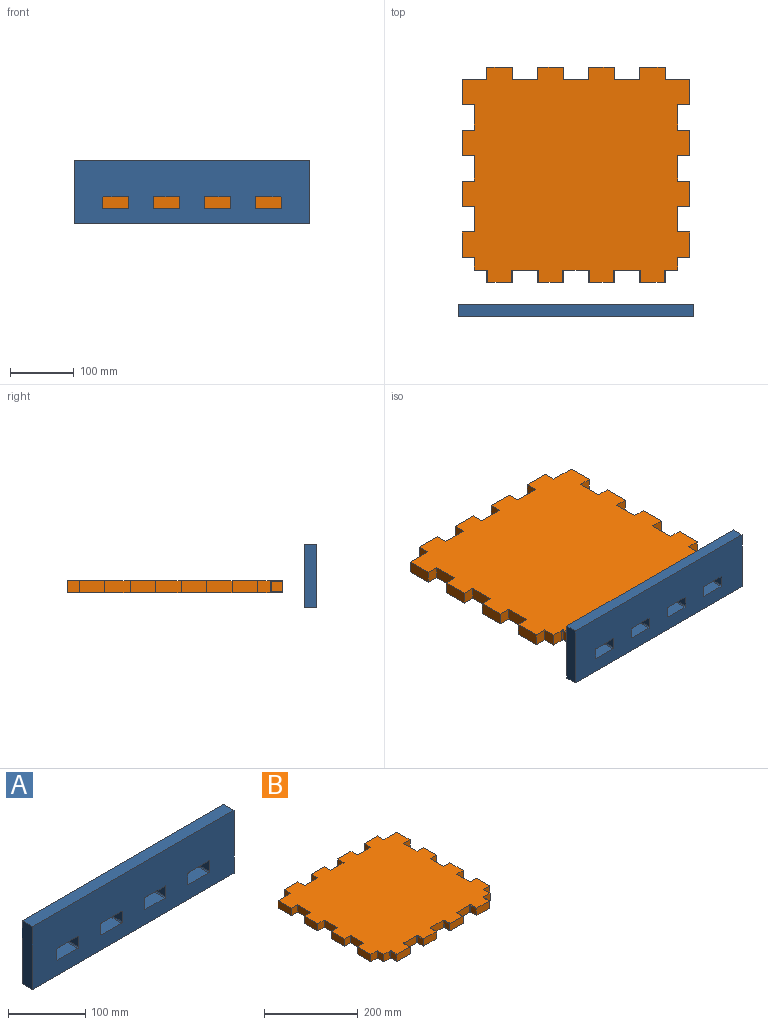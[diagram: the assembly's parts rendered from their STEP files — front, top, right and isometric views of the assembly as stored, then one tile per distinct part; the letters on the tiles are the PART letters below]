
ASSEMBLY  parts=2 mates=1
PART A: 64 faces, bbox 370x21.9x100 mm
  f0: plane 370x100mm, normal (0,-1,0), area 33967.7mm2, adj f2,f3,f4,f5,f6,f7,f8,f9
  f1: plane 370x100mm, normal (0,1,0), area 33733.9mm2, adj f2,f3,f4,f5,f6,f8,f10,f12
  f2: plane 370x19mm, normal (0,0,1), area 7030mm2, adj f0,f1,f3,f5
  f3: plane 100x19mm, normal (-1,0,0), area 1900mm2, adj f0,f1,f2,f4
  f4: plane 370x19mm, normal (0,0,-1), area 7030mm2, adj f0,f1,f3,f5
  f5: plane 100x19mm, normal (1,0,0), area 1900mm2, adj f0,f1,f2,f4
  f6: plane 37.8x19mm, normal (0,0,1), area 703.4mm2, adj f0,f1,f30,f31,f36,f37
  f7: plane 17.5x16mm, normal (-1,0,0), area 280mm2, adj f0,f28,f34,f36
  f8: plane 37.8x19mm, normal (0,0,-1), area 703.4mm2, adj f0,f1,f32,f33,f34,f35
  f9: plane 17.5x16mm, normal (1,0,0), area 280mm2, adj f0,f29,f30,f32
  f10: plane 37.8x19mm, normal (0,0,1), area 703.4mm2, adj f0,f1,f38,f39,f44,f45
  f11: plane 17.5x16mm, normal (-1,0,0), area 280mm2, adj f0,f26,f42,f44
  f12: plane 37.8x19mm, normal (0,0,-1), area 703.4mm2, adj f0,f1,f40,f41,f42,f43
  f13: plane 17.5x16mm, normal (1,0,0), area 280mm2, adj f0,f27,f38,f40
  f14: plane 37.8x19mm, normal (0,0,1), area 703.4mm2, adj f0,f1,f46,f47,f52,f53
  f15: plane 17.5x16mm, normal (-1,0,0), area 280mm2, adj f0,f24,f46,f48
  f16: plane 37.8x19mm, normal (0,0,-1), area 703.4mm2, adj f0,f1,f48,f49,f50,f51
  f17: plane 17.5x16mm, normal (1,0,0), area 280mm2, adj f0,f25,f50,f52
  f18: plane 37.8x19mm, normal (0,0,1), area 703.4mm2, adj f0,f1,f54,f55,f60,f61
  f19: plane 17.5x16mm, normal (-1,0,0), area 280mm2, adj f0,f22,f58,f60
  f20: plane 37.8x19mm, normal (0,0,-1), area 703.4mm2, adj f0,f1,f56,f57,f58,f59
  f21: plane 17.5x16mm, normal (1,0,0), area 280mm2, adj f0,f23,f54,f56
  f22: cylinder r=1.5mm len=16mm, axis (0,0,1), area 37.7mm2, adj f1,f19,f59,f61
  f23: cylinder r=1.5mm len=16mm, axis (0,0,-1), area 37.7mm2, adj f1,f21,f55,f57
  f24: cylinder r=1.5mm len=16mm, axis (0,0,1), area 37.7mm2, adj f1,f15,f47,f49
  f25: cylinder r=1.5mm len=16mm, axis (0,0,-1), area 37.7mm2, adj f1,f17,f51,f53
  f26: cylinder r=1.5mm len=16mm, axis (0,0,1), area 37.7mm2, adj f1,f11,f43,f45
  f27: cylinder r=1.5mm len=16mm, axis (0,0,-1), area 37.7mm2, adj f1,f13,f39,f41
  f28: cylinder r=1.5mm len=16mm, axis (0,0,1), area 37.7mm2, adj f1,f7,f35,f37
  f29: cylinder r=1.5mm len=16mm, axis (0,0,-1), area 37.7mm2, adj f1,f9,f31,f33
  f30: cylinder r=1.5mm len=17.5mm, axis (0,-1,0), area 41.2mm2, adj f0,f6,f9,f31
  f31: torus R=3mm, axis (0,0,1), area 4.2mm2, adj f1,f6,f29,f30
  f32: cylinder r=1.5mm len=17.5mm, axis (0,1,0), area 41.2mm2, adj f0,f8,f9,f33
  f33: torus R=3mm, axis (0,0,1), area 4.2mm2, adj f1,f8,f29,f32
  f34: cylinder r=1.5mm len=17.5mm, axis (0,-1,0), area 41.2mm2, adj f0,f7,f8,f35
  f35: torus R=3mm, axis (0,0,1), area 4.2mm2, adj f1,f8,f28,f34
  f36: cylinder r=1.5mm len=17.5mm, axis (0,1,0), area 41.2mm2, adj f0,f6,f7,f37
  f37: torus R=3mm, axis (0,0,1), area 4.2mm2, adj f1,f6,f28,f36
  f38: cylinder r=1.5mm len=17.5mm, axis (0,-1,0), area 41.2mm2, adj f0,f10,f13,f39
  f39: torus R=3mm, axis (0,0,1), area 4.2mm2, adj f1,f10,f27,f38
  f40: cylinder r=1.5mm len=17.5mm, axis (0,1,0), area 41.2mm2, adj f0,f12,f13,f41
  f41: torus R=3mm, axis (0,0,1), area 4.2mm2, adj f1,f12,f27,f40
  f42: cylinder r=1.5mm len=17.5mm, axis (0,-1,0), area 41.2mm2, adj f0,f11,f12,f43
  f43: torus R=3mm, axis (0,0,1), area 4.2mm2, adj f1,f12,f26,f42
  f44: cylinder r=1.5mm len=17.5mm, axis (0,1,0), area 41.2mm2, adj f0,f10,f11,f45
  f45: torus R=3mm, axis (0,0,1), area 4.2mm2, adj f1,f10,f26,f44
  f46: cylinder r=1.5mm len=17.5mm, axis (0,1,0), area 41.2mm2, adj f0,f14,f15,f47
  f47: torus R=3mm, axis (0,0,1), area 4.2mm2, adj f1,f14,f24,f46
  f48: cylinder r=1.5mm len=17.5mm, axis (0,-1,0), area 41.2mm2, adj f0,f15,f16,f49
  f49: torus R=3mm, axis (0,0,1), area 4.2mm2, adj f1,f16,f24,f48
  f50: cylinder r=1.5mm len=17.5mm, axis (0,1,0), area 41.2mm2, adj f0,f16,f17,f51
  f51: torus R=3mm, axis (0,0,1), area 4.2mm2, adj f1,f16,f25,f50
  f52: cylinder r=1.5mm len=17.5mm, axis (0,-1,0), area 41.2mm2, adj f0,f14,f17,f53
  f53: torus R=3mm, axis (0,0,1), area 4.2mm2, adj f1,f14,f25,f52
  f54: cylinder r=1.5mm len=17.5mm, axis (0,-1,0), area 41.2mm2, adj f0,f18,f21,f55
  f55: torus R=3mm, axis (0,0,1), area 4.2mm2, adj f1,f18,f23,f54
  f56: cylinder r=1.5mm len=17.5mm, axis (0,1,0), area 41.2mm2, adj f0,f20,f21,f57
  f57: torus R=3mm, axis (0,0,1), area 4.2mm2, adj f1,f20,f23,f56
  f58: cylinder r=1.5mm len=17.5mm, axis (0,-1,0), area 41.2mm2, adj f0,f19,f20,f59
  f59: torus R=3mm, axis (0,0,1), area 4.2mm2, adj f1,f20,f22,f58
  f60: cylinder r=1.5mm len=17.5mm, axis (0,1,0), area 41.2mm2, adj f0,f18,f19,f61
  f61: torus R=3mm, axis (0,0,1), area 4.2mm2, adj f1,f18,f22,f60
  f62: cylinder r=2.5mm len=5mm, axis (0,1,0), area 15.7mm2, adj f1,f63
  f63: plane 5x5mm, normal (0,1,0), area 19.6mm2, adj f62
PART B: 106 faces, bbox 358x338x24.8 mm
  f0: plane 19x19mm, normal (0,-1,0), area 361mm2, adj f1,f63,f64,f65
  f1: plane 20x19mm, normal (-1,0,0), area 380mm2, adj f0,f2,f64,f65
  f2: plane 19x18.9mm, normal (0,-1,0), area 351.9mm2, adj f1,f64,f65,f100,f101,f102
  f3: plane 17.5x16mm, normal (-1,0,0), area 280mm2, adj f4,f67,f75,f101
  f4: plane 40x19mm, normal (0,-1,0), area 758.1mm2, adj f3,f5,f64,f65,f66,f67,f74,f75
  f5: plane 17.5x16mm, normal (1,0,0), area 280mm2, adj f4,f66,f74,f104
  f6: plane 37.8x19mm, normal (0,-1,0), area 703.8mm2, adj f64,f65,f94,f95,f96,f103,f104,f105
  f7: plane 17.5x16mm, normal (-1,0,0), area 280mm2, adj f8,f69,f77,f95
  f8: plane 40x19mm, normal (0,-1,0), area 758.1mm2, adj f7,f9,f64,f65,f68,f69,f76,f77
  f9: plane 17.5x16mm, normal (1,0,0), area 280mm2, adj f8,f68,f76,f98
  f10: plane 37.8x19mm, normal (0,-1,0), area 703.8mm2, adj f64,f65,f88,f89,f90,f97,f98,f99
  f11: plane 17.5x16mm, normal (-1,0,0), area 280mm2, adj f12,f71,f79,f89
  f12: plane 40x19mm, normal (0,-1,0), area 758.1mm2, adj f11,f13,f64,f65,f70,f71,f78,f79
  f13: plane 17.5x16mm, normal (1,0,0), area 280mm2, adj f12,f70,f78,f92
  f14: plane 37.8x19mm, normal (0,-1,0), area 703.8mm2, adj f64,f65,f82,f83,f84,f91,f92,f93
  f15: plane 17.5x16mm, normal (-1,0,0), area 280mm2, adj f16,f73,f81,f83
  f16: plane 40x19mm, normal (0,-1,0), area 758.1mm2, adj f15,f17,f64,f65,f72,f73,f80,f81
  f17: plane 17.5x16mm, normal (1,0,0), area 280mm2, adj f16,f72,f80,f86
  f18: plane 19x18.9mm, normal (0,-1,0), area 351.9mm2, adj f19,f64,f65,f85,f86,f87
  f19: plane 20x19mm, normal (1,0,0), area 380mm2, adj f18,f20,f64,f65
  f20: plane 19x19mm, normal (0,-1,0), area 361mm2, adj f19,f21,f64,f65
  f21: plane 40x19mm, normal (1,0,0), area 760mm2, adj f20,f22,f64,f65
  f22: plane 19x19mm, normal (0,1,0), area 361mm2, adj f21,f23,f64,f65
  f23: plane 40x19mm, normal (1,0,0), area 760mm2, adj f22,f24,f64,f65
  f24: plane 19x19mm, normal (0,-1,0), area 361mm2, adj f23,f25,f64,f65
  f25: plane 40x19mm, normal (1,0,0), area 760mm2, adj f24,f26,f64,f65
  f26: plane 19x19mm, normal (0,1,0), area 361mm2, adj f25,f27,f64,f65
  f27: plane 40x19mm, normal (1,0,0), area 760mm2, adj f26,f28,f64,f65
  f28: plane 19x19mm, normal (0,-1,0), area 361mm2, adj f27,f29,f64,f65
  f29: plane 40x19mm, normal (1,0,0), area 760mm2, adj f28,f30,f64,f65
  f30: plane 19x19mm, normal (0,1,0), area 361mm2, adj f29,f31,f64,f65
  f31: plane 40x19mm, normal (1,0,0), area 760mm2, adj f30,f32,f64,f65
  f32: plane 19x19mm, normal (0,-1,0), area 361mm2, adj f31,f33,f64,f65
  f33: plane 40x19mm, normal (1,0,0), area 760mm2, adj f32,f34,f64,f65
  f34: plane 39x19mm, normal (0,1,0), area 741mm2, adj f33,f35,f64,f65
  f35: plane 19x19mm, normal (1,0,0), area 361mm2, adj f34,f36,f64,f65
  f36: plane 40x19mm, normal (0,1,0), area 760mm2, adj f35,f37,f64,f65
  f37: plane 19x19mm, normal (-1,0,0), area 361mm2, adj f36,f38,f64,f65
  f38: plane 40x19mm, normal (0,1,0), area 760mm2, adj f37,f39,f64,f65
  f39: plane 19x19mm, normal (1,0,0), area 361mm2, adj f38,f40,f64,f65
  f40: plane 40x19mm, normal (0,1,0), area 760mm2, adj f39,f41,f64,f65
  f41: plane 19x19mm, normal (-1,0,0), area 361mm2, adj f40,f42,f64,f65
  f42: plane 40x19mm, normal (0,1,0), area 760mm2, adj f41,f43,f64,f65
  f43: plane 19x19mm, normal (1,0,0), area 361mm2, adj f42,f44,f64,f65
  f44: plane 40x19mm, normal (0,1,0), area 760mm2, adj f43,f45,f64,f65
  f45: plane 19x19mm, normal (-1,0,0), area 361mm2, adj f44,f46,f64,f65
  f46: plane 40x19mm, normal (0,1,0), area 760mm2, adj f45,f47,f64,f65
  f47: plane 19x19mm, normal (1,0,0), area 361mm2, adj f46,f48,f64,f65
  f48: plane 40x19mm, normal (0,1,0), area 760mm2, adj f47,f49,f64,f65
  f49: plane 19x19mm, normal (-1,0,0), area 361mm2, adj f48,f50,f64,f65
  f50: plane 39x19mm, normal (0,1,0), area 741mm2, adj f49,f51,f64,f65
  f51: plane 40x19mm, normal (-1,0,0), area 760mm2, adj f50,f52,f64,f65
  f52: plane 19x19mm, normal (0,-1,0), area 361mm2, adj f51,f53,f64,f65
  f53: plane 40x19mm, normal (-1,0,0), area 760mm2, adj f52,f54,f64,f65
  f54: plane 19x19mm, normal (0,1,0), area 361mm2, adj f53,f55,f64,f65
  f55: plane 40x19mm, normal (-1,0,0), area 760mm2, adj f54,f56,f64,f65
  f56: plane 19x19mm, normal (0,-1,0), area 361mm2, adj f55,f57,f64,f65
  f57: plane 40x19mm, normal (-1,0,0), area 760mm2, adj f56,f58,f64,f65
  f58: plane 19x19mm, normal (0,1,0), area 361mm2, adj f57,f59,f64,f65
  f59: plane 40x19mm, normal (-1,0,0), area 760mm2, adj f58,f60,f64,f65
  f60: plane 19x19mm, normal (0,-1,0), area 361mm2, adj f59,f61,f64,f65
  f61: plane 40x19mm, normal (-1,0,0), area 760mm2, adj f60,f62,f64,f65
  f62: plane 19x19mm, normal (0,1,0), area 361mm2, adj f61,f63,f64,f65
  f63: plane 40x19mm, normal (-1,0,0), area 760mm2, adj f0,f62,f64,f65
  f64: plane 358x338mm, normal (0,0,1), area 107942.8mm2, adj f0,f1,f2,f4,f6,f8,f10,f12
  f65: plane 358x338mm, normal (0,0,-1), area 107942.8mm2, adj f0,f1,f2,f4,f6,f8,f10,f12
  f66: cylinder r=1.5mm len=17.5mm, axis (0,1,0), area 41.2mm2, adj f4,f5,f65,f103
  f67: cylinder r=1.5mm len=17.5mm, axis (0,-1,0), area 41.2mm2, adj f3,f4,f65,f100
  f68: cylinder r=1.5mm len=17.5mm, axis (0,1,0), area 41.2mm2, adj f8,f9,f65,f97
  f69: cylinder r=1.5mm len=17.5mm, axis (0,-1,0), area 41.2mm2, adj f7,f8,f65,f94
  f70: cylinder r=1.5mm len=17.5mm, axis (0,1,0), area 41.2mm2, adj f12,f13,f65,f91
  f71: cylinder r=1.5mm len=17.5mm, axis (0,-1,0), area 41.2mm2, adj f11,f12,f65,f88
  f72: cylinder r=1.5mm len=17.5mm, axis (0,1,0), area 41.2mm2, adj f16,f17,f65,f85
  f73: cylinder r=1.5mm len=17.5mm, axis (0,-1,0), area 41.2mm2, adj f15,f16,f65,f82
  f74: cylinder r=1.5mm len=17.5mm, axis (0,-1,0), area 41.2mm2, adj f4,f5,f64,f105
  f75: cylinder r=1.5mm len=17.5mm, axis (0,1,0), area 41.2mm2, adj f3,f4,f64,f102
  f76: cylinder r=1.5mm len=17.5mm, axis (0,-1,0), area 41.2mm2, adj f8,f9,f64,f99
  f77: cylinder r=1.5mm len=17.5mm, axis (0,1,0), area 41.2mm2, adj f7,f8,f64,f96
  f78: cylinder r=1.5mm len=17.5mm, axis (0,-1,0), area 41.2mm2, adj f12,f13,f64,f93
  f79: cylinder r=1.5mm len=17.5mm, axis (0,1,0), area 41.2mm2, adj f11,f12,f64,f90
  f80: cylinder r=1.5mm len=17.5mm, axis (0,-1,0), area 41.2mm2, adj f16,f17,f64,f87
  f81: cylinder r=1.5mm len=17.5mm, axis (0,1,0), area 41.2mm2, adj f15,f16,f64,f84
  f82: torus R=3mm, axis (0,1,0), area 4.2mm2, adj f14,f65,f73,f83
  f83: cylinder r=1.5mm len=16mm, axis (0,0,1), area 37.7mm2, adj f14,f15,f82,f84
  f84: torus R=3mm, axis (0,1,0), area 4.2mm2, adj f14,f64,f81,f83
  f85: torus R=3mm, axis (0,1,0), area 4.2mm2, adj f18,f65,f72,f86
  f86: cylinder r=1.5mm len=16mm, axis (0,0,-1), area 37.7mm2, adj f17,f18,f85,f87
  f87: torus R=3mm, axis (0,1,0), area 4.2mm2, adj f18,f64,f80,f86
  f88: torus R=3mm, axis (0,1,0), area 4.2mm2, adj f10,f65,f71,f89
  f89: cylinder r=1.5mm len=16mm, axis (0,0,1), area 37.7mm2, adj f10,f11,f88,f90
  f90: torus R=3mm, axis (0,1,0), area 4.2mm2, adj f10,f64,f79,f89
  f91: torus R=3mm, axis (0,1,0), area 4.2mm2, adj f14,f65,f70,f92
  f92: cylinder r=1.5mm len=16mm, axis (0,0,-1), area 37.7mm2, adj f13,f14,f91,f93
  f93: torus R=3mm, axis (0,1,0), area 4.2mm2, adj f14,f64,f78,f92
  f94: torus R=3mm, axis (0,1,0), area 4.2mm2, adj f6,f65,f69,f95
  f95: cylinder r=1.5mm len=16mm, axis (0,0,1), area 37.7mm2, adj f6,f7,f94,f96
  f96: torus R=3mm, axis (0,1,0), area 4.2mm2, adj f6,f64,f77,f95
  f97: torus R=3mm, axis (0,1,0), area 4.2mm2, adj f10,f65,f68,f98
  f98: cylinder r=1.5mm len=16mm, axis (0,0,-1), area 37.7mm2, adj f9,f10,f97,f99
  f99: torus R=3mm, axis (0,1,0), area 4.2mm2, adj f10,f64,f76,f98
  f100: torus R=3mm, axis (0,1,0), area 4.2mm2, adj f2,f65,f67,f101
  f101: cylinder r=1.5mm len=16mm, axis (0,0,1), area 37.7mm2, adj f2,f3,f100,f102
  f102: torus R=3mm, axis (0,1,0), area 4.2mm2, adj f2,f64,f75,f101
  f103: torus R=3mm, axis (0,1,0), area 4.2mm2, adj f6,f65,f66,f104
  f104: cylinder r=1.5mm len=16mm, axis (0,0,-1), area 37.7mm2, adj f5,f6,f103,f105
  f105: torus R=3mm, axis (0,1,0), area 4.2mm2, adj f6,f64,f74,f104
PLACE A t=(0,-29.33,0)mm
PLACE B at identity fixed
MATE slider A.f0 <-> B.f4  axis (0,-1,0) through (65,-48.33,19)mm
